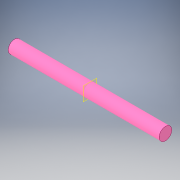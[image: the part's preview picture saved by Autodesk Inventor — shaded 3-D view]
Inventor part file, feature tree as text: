
AUTODESK INVENTOR PART (.ipt)
format: ipt  version: 2019.3 (Build 233278000, 278)  size: 90,624 bytes
history: native  units: in
note: dims shown in document units (in); Inventor stores cm internally (conversion verified against a paired STEP export)
features: extrude x1, sketch x1
ambient origin geometry x8: Origin, YZ Plane, XZ Plane, XY Plane, X Axis, Y Axis, Z Axis, Center Point
bodies: Solid1 (feature_tree)
feature tree (2):
  extrude  "Extrusion1"  Depth=3.0in TaperAngle=0.0deg
  sketch  "Sketch2"  dims[d0=0.25in d1=3.0in d2=0.0in]
